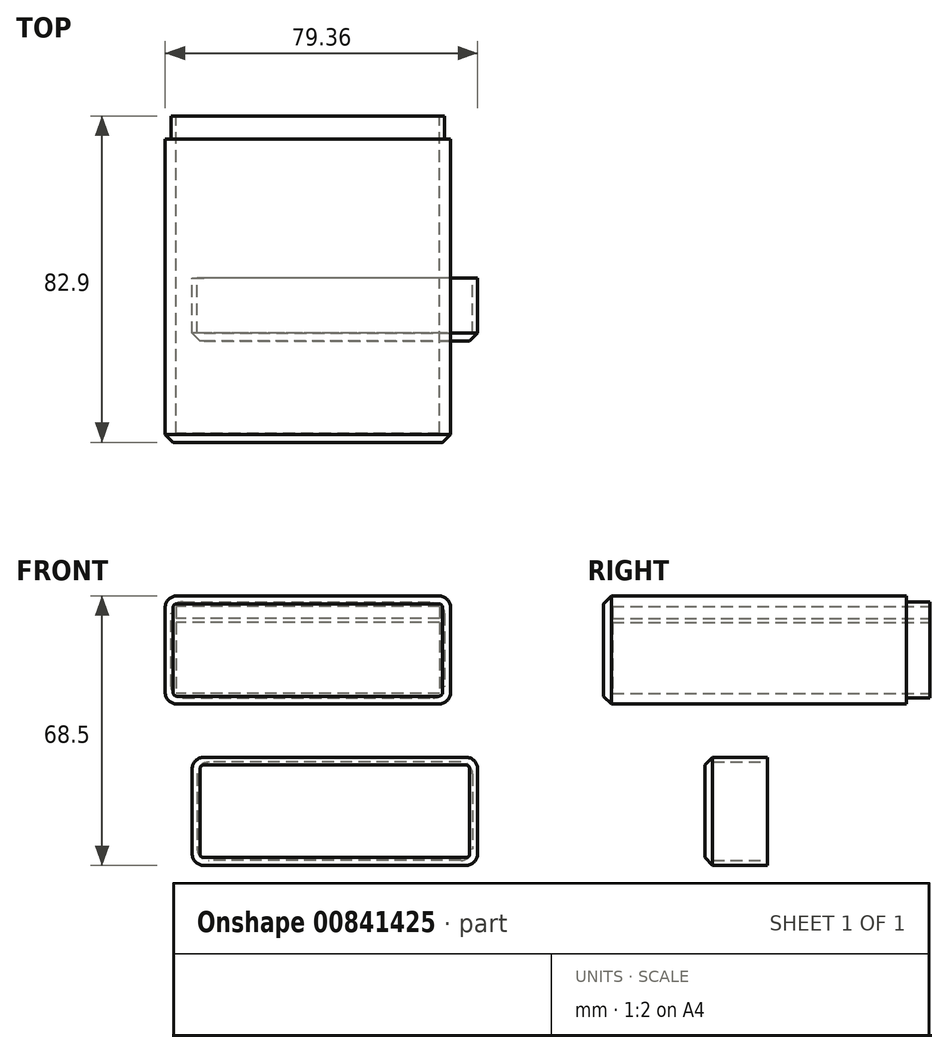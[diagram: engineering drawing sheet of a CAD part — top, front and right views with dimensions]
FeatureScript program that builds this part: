
annotation { "Feature Type Name" : "Feature", "Feature Type Description" : "" }
export const myFeature = defineFeature(function(context is Context, id is Id, definition is map)
    precondition{}
    {
        {
            var Q0;
            Q0=qCreatedBy(makeId("Top.planeOp"),FACE);
            var sketch = newSketch(context, id + "F0", { "sketchPlane" : qUnion([Q0])});
            skLineSegment(sketch, "E0.bottom", {"start": v(-41.61, 47.54) * mm, "end": v(27.89, 47.54) * mm});
            skLineSegment(sketch, "E0.top", {"start": v(-41.61, -41.71) * mm, "end": v(27.89, -41.71) * mm});
            skLineSegment(sketch, "E0.left", {"start": v(-41.61, 47.54) * mm, "end": v(-41.61, -41.71) * mm});
            skLineSegment(sketch, "E0.right", {"start": v(27.89, 47.54) * mm, "end": v(27.89, -41.71) * mm});
            skSolve(sketch);
        }
        {
            var Q0;
            Q0=makeQuery(id+"F0.imprint","IMPRINT",FACE,{"disambiguationData":[TD([[makeQuery(id+"F0.imprint","IMPRINT",EDGE,{"derivedFrom":sQuery(id+"F0.wireOp",EDGE,"E0.bottom")}),-1.0]])]});
            extrude(context, id + "F1", {"entities" : qUnion([Q0]), "depth" : 24.5 * mm, "offsetDistance" : 25 * mm});
        }
        {
            var Q0;
            Q0=makeQuery(id+"F1.opExtrude","SWEPT_FACE",FACE,{"disambiguationData":[OSD([sQuery(id+"F0.wireOp",EDGE,"E0.bottom")])]});
            var sketch = newSketch(context, id + "F2", { "sketchPlane" : qUnion([Q0])});
            skLineSegment(sketch, "E1.bottom", {"start": v(-26.64, 19.25) * mm, "end": v(40.36, 19.25) * mm});
            skLineSegment(sketch, "E1.top", {"start": v(-26.64, 1.25) * mm, "end": v(40.36, 1.25) * mm});
            skLineSegment(sketch, "E1.left", {"start": v(-26.64, 19.25) * mm, "end": v(-26.64, 1.25) * mm});
            skLineSegment(sketch, "E1.right", {"start": v(40.36, 19.25) * mm, "end": v(40.36, 1.25) * mm});
            skSolve(sketch);
        }
        {
            var Q0;
            Q0 = qSketchRegion(id + "F2", true);
            extrude(context, id + "F3", {"entities" : qUnion([Q0]), "operationType" : NewBodyOperationType.REMOVE, "oppositeDirection" : true, "depth" : 87 * mm, "offsetDistance" : 25 * mm});
        }
        {
            var Q0;
            Q0=makeQuery(id+"F1.opExtrude","SWEPT_FACE",FACE,{"disambiguationData":[OSD([sQuery(id+"F0.wireOp",EDGE,"E0.bottom")])]});
            var sketch = newSketch(context, id + "F4", { "sketchPlane" : qUnion([Q0])});
            skLineSegment(sketch, "E2.bottom", {"start": v(-26.64, 23.25) * mm, "end": v(40.36, 23.25) * mm});
            skLineSegment(sketch, "E2.top", {"start": v(-26.64, 20.25) * mm, "end": v(40.36, 20.25) * mm});
            skLineSegment(sketch, "E2.left", {"start": v(-26.64, 23.25) * mm, "end": v(-26.64, 20.25) * mm});
            skLineSegment(sketch, "E2.right", {"start": v(40.36, 23.25) * mm, "end": v(40.36, 20.25) * mm});
            skSolve(sketch);
        }
        {
            var Q0;
            Q0=makeQuery(id+"F4.imprint","IMPRINT",FACE,{"disambiguationData":[TD([[makeQuery(id+"F4.imprint","IMPRINT",EDGE,{"derivedFrom":sQuery(id+"F4.wireOp",EDGE,"kL87RSZs-Uyr2-qjcC-7kU0-fd4pUUnYQ4zQ.bottom")}),-1.0]])]});
            var Q1;
            Q1=makeQuery(id+"F4.imprint","IMPRINT",FACE,{"disambiguationData":[TD([[makeQuery(id+"F4.imprint","IMPRINT",EDGE,{"derivedFrom":sQuery(id+"F4.wireOp",EDGE,"E2.bottom")}),-1.0]])]});
            extrude(context, id + "F5", {"entities" : qUnion([Q0, Q1]), "operationType" : NewBodyOperationType.REMOVE, "oppositeDirection" : true, "depth" : 87 * mm, "offsetDistance" : 25 * mm});
        }
        {
            var Q0;
            Q0=makeQuery(id+"F1.opExtrude","SWEPT_FACE",FACE,{"disambiguationData":[OSD([sQuery(id+"F0.wireOp",EDGE,"E0.top")])]});
            var sketch = newSketch(context, id + "F6", { "sketchPlane" : qUnion([Q0])});
            skLineSegment(sketch, "E3.bottom", {"start": v(-43.11, 26) * mm, "end": v(29.39, 26) * mm});
            skLineSegment(sketch, "E3.top", {"start": v(-43.11, -1.5) * mm, "end": v(29.39, -1.5) * mm});
            skLineSegment(sketch, "E3.left", {"start": v(-43.11, 26) * mm, "end": v(-43.11, -1.5) * mm});
            skLineSegment(sketch, "E3.right", {"start": v(29.39, 26) * mm, "end": v(29.39, -1.5) * mm});
            skPoint(sketch, "E4", {"position": v(-6.86, -1.5) * mm});
            skPoint(sketch, "E5", {"position": v(-43.11, 12.25) * mm});
            skSolve(sketch);
        }
        {
            var Q0;
            Q0=makeQuery(id+"F6.imprint","IMPRINT",FACE,{"disambiguationData":[TD([[makeQuery(id+"F6.imprint","IMPRINT",EDGE,{"derivedFrom":sQuery(id+"F6.wireOp",EDGE,"E3.bottom")}),-1.0]])]});
            extrude(context, id + "F7", {"entities" : qUnion([Q0]), "operationType" : NewBodyOperationType.ADD, "oppositeDirection" : true, "depth" : (92 - 15) * mm, "offsetDistance" : 25 * mm});
        }
        {
            var Q0;
            Q0=makeQuery(id+"F1.opExtrude","SWEPT_FACE",FACE,{"disambiguationData":[OSD([sQuery(id+"F0.wireOp",EDGE,"E0.right")])]});
            var sketch = newSketch(context, id + "F8", { "sketchPlane" : qUnion([Q0])});
            skLineSegment(sketch, "E6.bottom", {"start": v(47.54, 24.5) * mm, "end": v(41.19, 24.5) * mm});
            skLineSegment(sketch, "E6.top", {"start": v(47.54, 0) * mm, "end": v(41.19, 0) * mm});
            skLineSegment(sketch, "E6.left", {"start": v(47.54, 24.5) * mm, "end": v(47.54, 0) * mm});
            skLineSegment(sketch, "E6.right", {"start": v(41.19, 24.5) * mm, "end": v(41.19, 0) * mm});
            skSolve(sketch);
        }
        {
            var Q0;
            Q0=makeQuery(id+"F8.imprint","IMPRINT",FACE,{"disambiguationData":[TD([[makeQuery(id+"F8.imprint","IMPRINT",EDGE,{"derivedFrom":sQuery(id+"F8.wireOp",EDGE,"E6.bottom")}),1.0]])]});
            var Q1;
            Q1=makeQuery(id+"F1.opExtrude","SWEPT_FACE",FACE,{"disambiguationData":[OSD([sQuery(id+"F0.wireOp",EDGE,"E0.left")])]});
            extrude(context, id + "F9", {"entities" : qUnion([Q0, Q1]), "operationType" : NewBodyOperationType.REMOVE, "oppositeDirection" : true, "depth" : 70 * mm, "offsetDistance" : 25 * mm});
        }
        {
            var Q0;
            Q0=qCreatedBy(makeId("Front.planeOp"),FACE);
            var sketch = newSketch(context, id + "F10", { "sketchPlane" : qUnion([Q0])});
            skLineSegment(sketch, "E7.bottom", {"start": v(36.25, -15) * mm, "end": v(-36.25, -15) * mm});
            skLineSegment(sketch, "E7.top", {"start": v(36.25, -42.5) * mm, "end": v(-36.25, -42.5) * mm});
            skLineSegment(sketch, "E7.left", {"start": v(36.25, -15) * mm, "end": v(36.25, -42.5) * mm});
            skLineSegment(sketch, "E7.right", {"start": v(-36.25, -15) * mm, "end": v(-36.25, -42.5) * mm});
            skPoint(sketch, "E8", {"position": v(0, -15) * mm});
            skSolve(sketch);
        }
        {
            var Q0;
            Q0=makeQuery(id+"F10.imprint","IMPRINT",FACE,{"disambiguationData":[TD([[makeQuery(id+"F10.imprint","IMPRINT",EDGE,{"derivedFrom":sQuery(id+"F10.wireOp",EDGE,"E7.bottom")}),1.0]])]});
            extrude(context, id + "F11", {"entities" : qUnion([Q0]), "depth" : 16 * mm, "offsetDistance" : 25 * mm});
        }
        {
            var Q0;
            Q0=makeQuery(id+"F11.opExtrude","CAP_FACE",FACE,{"disambiguationData":[OSD([sQuery(id+"F10.wireOp",EDGE,"E7.bottom"),sQuery(id+"F10.wireOp",EDGE,"E7.top"),sQuery(id+"F10.wireOp",EDGE,"E7.left"),sQuery(id+"F10.wireOp",EDGE,"E7.right")])],"isStart":true});
            var sketch = newSketch(context, id + "F12", { "sketchPlane" : qUnion([Q0])});
            skLineSegment(sketch, "E9.bottom", {"start": v(-35, -16.25) * mm, "end": v(35, -16.25) * mm});
            skLineSegment(sketch, "E9.top", {"start": v(-35, -41.25) * mm, "end": v(35, -41.25) * mm});
            skLineSegment(sketch, "E9.left", {"start": v(-35, -16.25) * mm, "end": v(-35, -41.25) * mm});
            skLineSegment(sketch, "E9.right", {"start": v(35, -16.25) * mm, "end": v(35, -41.25) * mm});
            skPoint(sketch, "E10", {"position": v(0, -16.25) * mm});
            skPoint(sketch, "E11", {"position": v(-35, -28.75) * mm});
            skSolve(sketch);
        }
        {
            var Q0;
            Q0=makeQuery(id+"F12.imprint","IMPRINT",FACE,{"disambiguationData":[TD([[makeQuery(id+"F12.imprint","IMPRINT",EDGE,{"derivedFrom":sQuery(id+"F12.wireOp",EDGE,"E9.bottom")}),-1.0]])]});
            extrude(context, id + "F13", {"entities" : qUnion([Q0]), "operationType" : NewBodyOperationType.REMOVE, "oppositeDirection" : true, "depth" : 14 * mm, "offsetDistance" : 25 * mm});
        }
        {
            var Q0;
            Q0=makeQuery(id+"F11.opExtrude","SWEPT_EDGE",EDGE,{"disambiguationData":[OSD([sQuery(id+"F10.wireOp",EDGE,"E7.top"),sQuery(id+"F10.wireOp",EDGE,"E7.left")])]});
            var Q1;
            Q1=makeQuery(id+"F11.opExtrude","SWEPT_EDGE",EDGE,{"disambiguationData":[OSD([sQuery(id+"F10.wireOp",EDGE,"E7.top"),sQuery(id+"F10.wireOp",EDGE,"E7.right")])]});
            var Q2;
            Q2=makeQuery(id+"F11.opExtrude","SWEPT_EDGE",EDGE,{"disambiguationData":[OSD([sQuery(id+"F10.wireOp",EDGE,"E7.bottom"),sQuery(id+"F10.wireOp",EDGE,"E7.right")])]});
            var Q3;
            Q3=makeQuery(id+"F11.opExtrude","SWEPT_EDGE",EDGE,{"disambiguationData":[OSD([sQuery(id+"F10.wireOp",EDGE,"E7.bottom"),sQuery(id+"F10.wireOp",EDGE,"E7.left")])]});
            fillet(context, id + "F14", {"entities" : qUnion([Q0, Q1, Q2, Q3]), "radius" : 3 * mm, "tangentPropagation" : true, "allowEdgeOverflow" : false});
        }
        {
            var Q0;
            Q0=makeQuery(id+"F11.opExtrude","CAP_EDGE",EDGE,{"disambiguationData":[OSD([sQuery(id+"F10.wireOp",EDGE,"E7.top")])],"isStart":false});
            chamfer(context, id + "F15", {"entities" : qUnion([Q0]), "width" : 2 * mm, "tangentPropagation" : true});
        }
        {
            var Q0;
            Q0=makeQuery(id+"F7.opExtrude","SWEPT_EDGE",EDGE,{"disambiguationData":[OSD([sQuery(id+"F6.wireOp",EDGE,"E3.top"),sQuery(id+"F6.wireOp",EDGE,"E3.right")])]});
            var Q1;
            Q1=makeQuery(id+"F7.opExtrude","SWEPT_EDGE",EDGE,{"disambiguationData":[OSD([sQuery(id+"F6.wireOp",EDGE,"E3.bottom"),sQuery(id+"F6.wireOp",EDGE,"E3.right")])]});
            var Q2;
            Q2=makeQuery(id+"F7.opExtrude","SWEPT_EDGE",EDGE,{"disambiguationData":[OSD([sQuery(id+"F6.wireOp",EDGE,"E3.top"),sQuery(id+"F6.wireOp",EDGE,"E3.left")])]});
            var Q3;
            Q3=makeQuery(id+"F7.opExtrude","SWEPT_EDGE",EDGE,{"disambiguationData":[OSD([sQuery(id+"F6.wireOp",EDGE,"E3.bottom"),sQuery(id+"F6.wireOp",EDGE,"E3.left")])]});
            fillet(context, id + "F16", {"entities" : qUnion([Q0, Q1, Q2, Q3]), "radius" : 3 * mm, "tangentPropagation" : true, "allowEdgeOverflow" : false});
        }
        {
            var Q0;
            {var subQ0=sQuery(id+"F0.wireOp",EDGE,"E0.top");Q0=makeQuery(id+"F7.boolean.opBoolean","MERGE",FACE,{"derivedFrom":[makeQuery(id+"F1.opExtrude","SWEPT_FACE",FACE,{"disambiguationData":[OSD([subQ0])]}),makeQuery(id+"F7.opExtrude","CAP_FACE",FACE,{"disambiguationData":[OSD([subQ0,sQuery(id+"F0.wireOp",EDGE,"E0.left"),sQuery(id+"F0.wireOp",EDGE,"E0.right"),sQuery(id+"F6.wireOp",EDGE,"E3.bottom"),sQuery(id+"F6.wireOp",EDGE,"E3.top"),sQuery(id+"F6.wireOp",EDGE,"E3.left"),sQuery(id+"F6.wireOp",EDGE,"E3.right")])],"isStart":true})]});}
            chamfer(context, id + "F17", {"entities" : qUnion([Q0]), "width" : 2 * mm, "tangentPropagation" : true});
        }
        {
            var Q0;
            Q0=makeQuery(id+"F1.opExtrude","CAP_EDGE",EDGE,{"disambiguationData":[OSD([sQuery(id+"F0.wireOp",EDGE,"E0.left")])],"isStart":false});
            var Q1;
            Q1=makeQuery(id+"F1.opExtrude","CAP_EDGE",EDGE,{"disambiguationData":[OSD([sQuery(id+"F0.wireOp",EDGE,"E0.right")])],"isStart":false});
            var Q2;
            Q2=makeQuery(id+"F1.opExtrude","CAP_EDGE",EDGE,{"disambiguationData":[OSD([sQuery(id+"F0.wireOp",EDGE,"E0.left")])],"isStart":true});
            var Q3;
            Q3=makeQuery(id+"F1.opExtrude","CAP_EDGE",EDGE,{"disambiguationData":[OSD([sQuery(id+"F0.wireOp",EDGE,"E0.right")])],"isStart":true});
            fillet(context, id + "F18", {"entities" : qUnion([Q0, Q1, Q2, Q3]), "radius" : 3 * mm, "tangentPropagation" : true, "allowEdgeOverflow" : false});
        }
        {
            var Q0;
            Q0=makeQuery(id+"F13.boolean.opBoolean","COPY",EDGE,{"derivedFrom":makeQuery(id+"F13.opExtrude","SWEPT_EDGE",EDGE,{"disambiguationData":[OSD([sQuery(id+"F12.wireOp",EDGE,"E9.bottom"),sQuery(id+"F12.wireOp",EDGE,"E9.right")])]})});
            var Q1;
            Q1=makeQuery(id+"F13.boolean.opBoolean","COPY",EDGE,{"derivedFrom":makeQuery(id+"F13.opExtrude","SWEPT_EDGE",EDGE,{"disambiguationData":[OSD([sQuery(id+"F12.wireOp",EDGE,"E9.bottom"),sQuery(id+"F12.wireOp",EDGE,"E9.left")])]})});
            var Q2;
            Q2=makeQuery(id+"F13.boolean.opBoolean","COPY",EDGE,{"derivedFrom":makeQuery(id+"F13.opExtrude","SWEPT_EDGE",EDGE,{"disambiguationData":[OSD([sQuery(id+"F12.wireOp",EDGE,"E9.top"),sQuery(id+"F12.wireOp",EDGE,"E9.right")])]})});
            var Q3;
            Q3=makeQuery(id+"F13.boolean.opBoolean","COPY",EDGE,{"derivedFrom":makeQuery(id+"F13.opExtrude","SWEPT_EDGE",EDGE,{"disambiguationData":[OSD([sQuery(id+"F12.wireOp",EDGE,"E9.top"),sQuery(id+"F12.wireOp",EDGE,"E9.left")])]})});
            fillet(context, id + "F19", {"entities" : qUnion([Q0, Q1, Q2, Q3]), "radius" : 3 * mm, "tangentPropagation" : true, "allowEdgeOverflow" : false});
        }
    });
